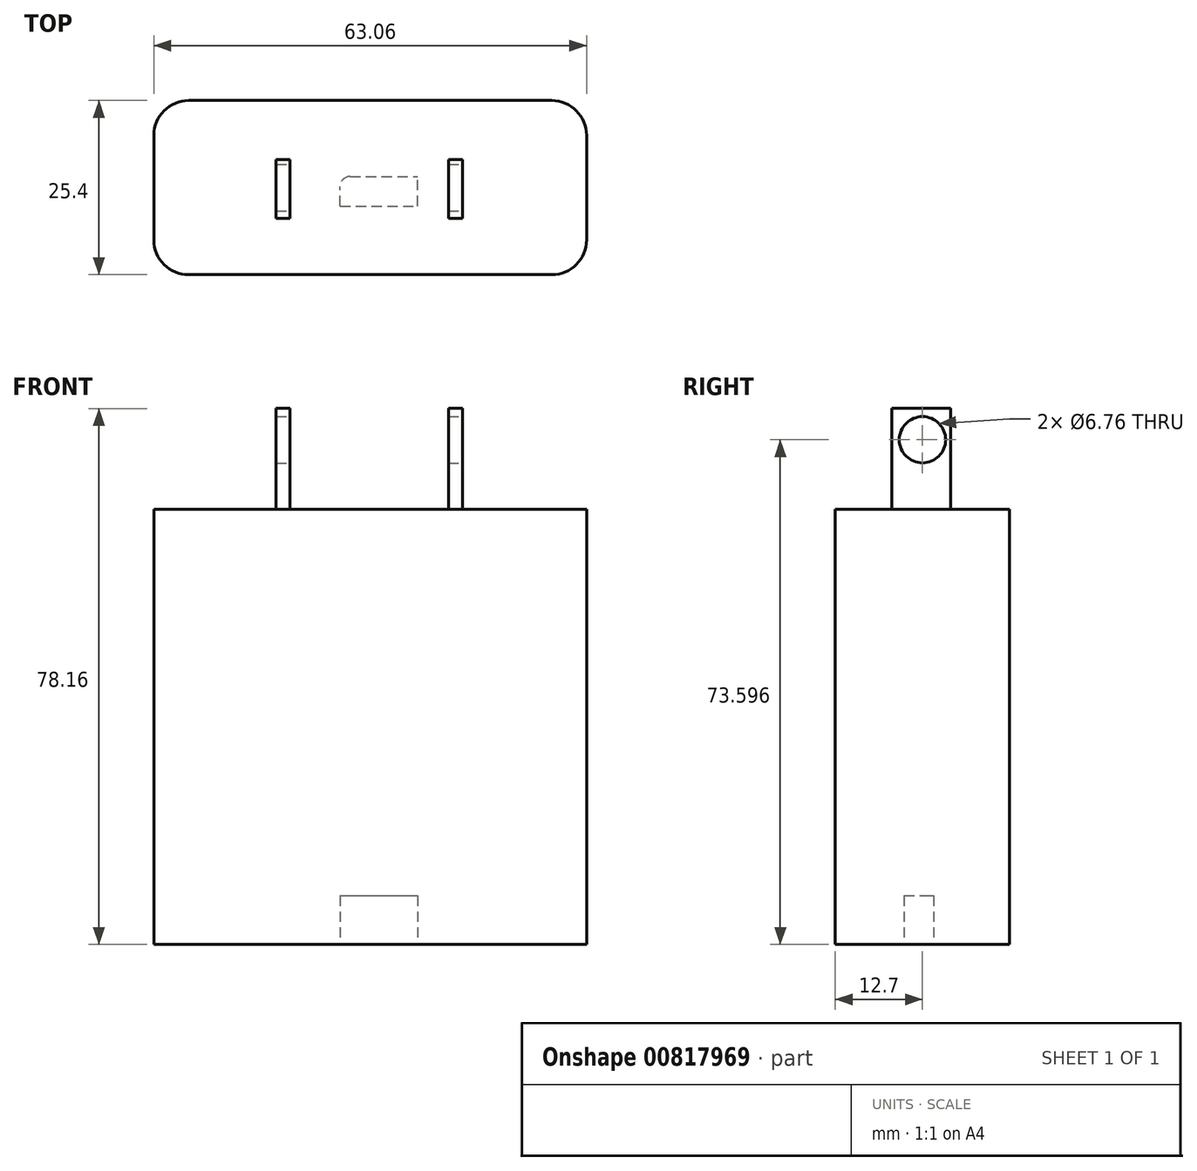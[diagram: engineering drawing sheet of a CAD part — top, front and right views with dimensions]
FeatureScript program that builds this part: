
annotation { "Feature Type Name" : "Feature", "Feature Type Description" : "" }
export const myFeature = defineFeature(function(context is Context, id is Id, definition is map)
    precondition{}
    {
        {
            var Q0;
            Q0=qCreatedBy(makeId("Front.planeOp"),FACE);
            var sketch = newSketch(context, id + "F0", { "sketchPlane" : qUnion([Q0])});
            skLineSegment(sketch, "E0.bottom", {"start": v(-36.03, 24.83) * mm, "end": v(27.03, 24.83) * mm});
            skLineSegment(sketch, "E0.top", {"start": v(-36.03, -38.6) * mm, "end": v(27.03, -38.6) * mm});
            skLineSegment(sketch, "E0.left", {"start": v(-36.03, 24.83) * mm, "end": v(-36.03, -38.6) * mm});
            skLineSegment(sketch, "E0.right", {"start": v(27.03, 24.83) * mm, "end": v(27.03, -38.6) * mm});
            skSolve(sketch);
        }
        {
            var Q0;
            Q0=makeQuery(id+"F0.imprint","IMPRINT",FACE,{"disambiguationData":[TD([[makeQuery(id+"F0.imprint","IMPRINT",EDGE,{"derivedFrom":sQuery(id+"F0.wireOp",EDGE,"E0.bottom")}),-1.0]])]});
            extrude(context, id + "F1", {"entities" : qUnion([Q0]), "endBound" : BoundingType.SYMMETRIC, "depth" : 25.4 * mm, "offsetDistance" : 25.4 * mm});
        }
        {
            var Q0;
            Q0=makeQuery(id+"F1.opExtrude","CAP_EDGE",EDGE,{"disambiguationData":[OSD([sQuery(id+"F0.wireOp",EDGE,"E0.right")])],"isStart":false});
            var Q1;
            Q1=makeQuery(id+"F1.opExtrude","CAP_EDGE",EDGE,{"disambiguationData":[OSD([sQuery(id+"F0.wireOp",EDGE,"E0.right")])],"isStart":true});
            var Q2;
            Q2=makeQuery(id+"F1.opExtrude","CAP_EDGE",EDGE,{"disambiguationData":[OSD([sQuery(id+"F0.wireOp",EDGE,"E0.left")])],"isStart":true});
            var Q3;
            Q3=makeQuery(id+"F1.opExtrude","CAP_EDGE",EDGE,{"disambiguationData":[OSD([sQuery(id+"F0.wireOp",EDGE,"E0.left")])],"isStart":false});
            fillet(context, id + "F2", {"entities" : qUnion([Q0, Q1, Q2, Q3]), "radius" : 5.08 * mm, "tangentPropagation" : true, "allowEdgeOverflow" : false});
        }
        {
            var Q0;
            Q0=makeQuery(id+"F1.opExtrude","SWEPT_FACE",FACE,{"disambiguationData":[OSD([sQuery(id+"F0.wireOp",EDGE,"E0.bottom")])]});
            var sketch = newSketch(context, id + "F3", { "sketchPlane" : qUnion([Q0])});
            skLineSegment(sketch, "E1", {"start": v(-16.2, 4.07) * mm, "end": v(-16.2, -4.46) * mm});
            skLineSegment(sketch, "E2", {"start": v(6.89, 4.07) * mm, "end": v(6.89, -4.46) * mm});
            skSolve(sketch);
        }
        {
            var Q0;
            Q0=sQuery(id+"F3.wireOp",EDGE,"E1");
            var Q1;
            Q1=sQuery(id+"F3.wireOp",EDGE,"E2");
            extrude(context, id + "F4", {"bodyType" : ToolBodyType.SURFACE, "surfaceEntities" : qUnion([Q0, Q1]), "depth" : 14.73 * mm, "offsetDistance" : 25.4 * mm});
        }
        {
            var Q0;
            Q0=makeQuery(id+"F4.opExtrude","SWEPT_FACE",FACE,{"disambiguationData":[OSD([sQuery(id+"F3.wireOp",EDGE,"E1")])]});
            extrude(context, id + "F5", {"entities" : qUnion([Q0]), "operationType" : NewBodyOperationType.ADD, "depth" : 2.03 * mm, "offsetDistance" : 25.4 * mm});
        }
        {
            var Q0;
            Q0=makeQuery(id+"F4.opExtrude","SWEPT_FACE",FACE,{"disambiguationData":[OSD([sQuery(id+"F3.wireOp",EDGE,"E2")])]});
            extrude(context, id + "F6", {"entities" : qUnion([Q0]), "operationType" : NewBodyOperationType.ADD, "oppositeDirection" : true, "depth" : 2.03 * mm, "offsetDistance" : 25.4 * mm});
        }
        {
            var Q0;
            Q0=makeQuery(id+"F6.opExtrude","CAP_FACE",FACE,{"disambiguationData":[OSD([sQuery(id+"F3.wireOp",EDGE,"E2")])],"isStart":false});
            var sketch = newSketch(context, id + "F7", { "sketchPlane" : qUnion([Q0])});
            skCircle(sketch, "E3", {"center": v(0, 35) * mm, "radius": 2.16 * mm});
            skSolve(sketch);
        }
        {
            var Q0;
            Q0=sQuery(id+"F7.wireOp",VERTEX,"E3.center");
            var Q1;
            Q1=makeQuery(id+"F1.opExtrude","SWEPT_BODY",BODY,{"disambiguationData":[OSD([sQuery(id+"F0.wireOp",EDGE,"E0.bottom"),sQuery(id+"F0.wireOp",EDGE,"E0.top"),sQuery(id+"F0.wireOp",EDGE,"E0.left"),sQuery(id+"F0.wireOp",EDGE,"E0.right")])]});
            hole(context, id + "F8", {"style" : HoleStyle.SIMPLE, "endStyle" : HoleEndStyle.THROUGH, "holeDiameter" : 6.76 * mm, "majorDiameter" : 6.35 * mm, "isTappedThrough" : true, "tappedDepth" : 12.7 * mm, "tapClearance" : 3, "locations" : qUnion([Q0]), "scope" : qUnion([Q1])});
        }
        {
            var Q0;
            Q0=makeQuery(id+"F1.opExtrude","SWEPT_FACE",FACE,{"disambiguationData":[OSD([sQuery(id+"F0.wireOp",EDGE,"E0.top")])]});
            var sketch = newSketch(context, id + "F9", { "sketchPlane" : qUnion([Q0])});
            skLineSegment(sketch, "E4.bottom", {"start": v(-8.9, 2.68) * mm, "end": v(2.4, 2.68) * mm});
            skLineSegment(sketch, "E4.top", {"start": v(-8.9, -1.61) * mm, "end": v(2.4, -1.61) * mm});
            skLineSegment(sketch, "E4.left", {"start": v(-8.9, 2.68) * mm, "end": v(-8.9, -1.61) * mm});
            skLineSegment(sketch, "E4.right", {"start": v(2.4, 2.68) * mm, "end": v(2.4, -1.61) * mm});
            skSolve(sketch);
        }
        {
            var Q0;
            Q0=makeQuery(id+"F9.imprint","IMPRINT",FACE,{"disambiguationData":[TD([[makeQuery(id+"F9.imprint","IMPRINT",EDGE,{"derivedFrom":sQuery(id+"F9.wireOp",EDGE,"E4.bottom")}),-1.0]])]});
            extrude(context, id + "F10", {"entities" : qUnion([Q0]), "operationType" : NewBodyOperationType.REMOVE, "oppositeDirection" : true, "depth" : 7.11 * mm, "offsetDistance" : 25.4 * mm});
        }
        {
            var Q0;
            Q0=makeQuery(id+"F10.boolean.opBoolean","COPY",EDGE,{"derivedFrom":makeQuery(id+"F10.opExtrude","SWEPT_EDGE",EDGE,{"disambiguationData":[OSD([sQuery(id+"F9.wireOp",EDGE,"E4.top"),sQuery(id+"F9.wireOp",EDGE,"E4.left")])]})});
            fillet(context, id + "F11", {"entities" : qUnion([Q0]), "radius" : 1.47 * mm, "allowEdgeOverflow" : false});
        }
    });
